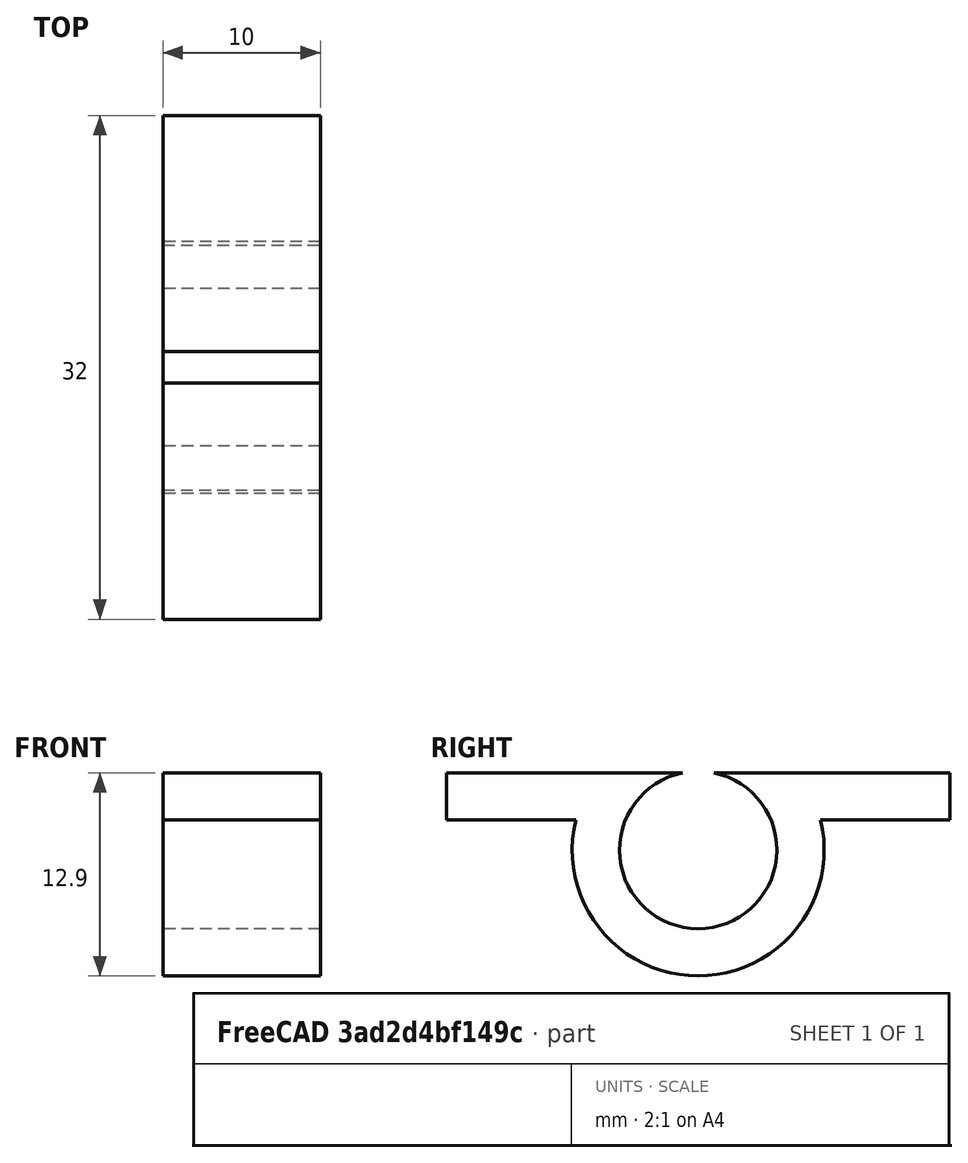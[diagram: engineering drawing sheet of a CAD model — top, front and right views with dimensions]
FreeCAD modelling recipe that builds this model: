
FCSTD DOCUMENT  (FreeCAD 0.16R6703 (Git))
Label: seesaw_hinge
License: Public Domain
LicenseURL: http://en.wikipedia.org/wiki/Public_domain
objects: Sketcher::SketchObject×1, PartDesign::Pad×1
note: 3 computed .brp shape members not serialized (recipe doc carries the construction recipe); baked Part::Feature solids carry a one-line shape summary decoded from their .brp

FEATURE [Sketcher::SketchObject] Sketch
  Placement = pos=(0,0,0) rot=(0.57735,0.57735,0.57735;2.0944rad)
  sketch-geometry (13):
    g0: ArcOfCircle CenterX=0 CenterY=-4.89898 CenterZ=0 NormalX=0 NormalY=0 NormalZ=1 Radius=5 StartAngle=1.77215 EndAngle=7.65262
    g1: LineSegment StartX=-1 StartY=0 StartZ=0 EndX=-16 EndY=0 EndZ=0
    g2: LineSegment StartX=-16 StartY=0 StartZ=0 EndX=-16 EndY=-3 EndZ=0
    g3: LineSegment StartX=-16 StartY=-3 StartZ=0 EndX=-7.77135 EndY=-3 EndZ=0
    g4: LineSegment StartX=1 StartY=0 StartZ=0 EndX=16 EndY=0 EndZ=0
    g5: LineSegment StartX=16 StartY=0 StartZ=0 EndX=16 EndY=-3 EndZ=0
    g6: LineSegment StartX=16 StartY=-3 StartZ=0 EndX=7.77135 EndY=-3 EndZ=0
    g7: ArcOfCircle CenterX=0 CenterY=-4.89898 CenterZ=0 NormalX=0 NormalY=0 NormalZ=1 Radius=8 StartAngle=2.90193 EndAngle=6.52285
    g8: LineSegment [constr] StartX=-1 StartY=0 StartZ=0 EndX=1 EndY=0 EndZ=0
    g9: GeomPoint [constr] X=-3.47116 Y=-8.49773 Z=0
    g10: LineSegment [constr] StartX=0 StartY=-4.89898 StartZ=0 EndX=-3.47116 EndY=-8.49773 EndZ=0
    g11: LineSegment [constr] StartX=-3.47116 StartY=-8.49773 StartZ=0 EndX=-5.55386 EndY=-10.657 EndZ=0
    g12: LineSegment [constr] StartX=0 StartY=-4.89898 StartZ=0 EndX=0 EndY=0 EndZ=0
  constraints (35):
    c: Coincident(g1,g0)
    c: Coincident(g2,g1)
    c: Coincident(g3,g2)
    c: Coincident(g4,g0)
    c: Coincident(g5,g4)
    c: Coincident(g6,g5)
    c: Coincident(g7,g0)
    c: Coincident(g7,g3)
    c: Coincident(g7,g6)
    c: Horizontal(g1)
    c: Horizontal(g4)
    c: Horizontal(g6)
    c: Horizontal(g3)
    c: Vertical(g2)
    c: Vertical(g5)
    c: Equal(g5,g2)
    c: Equal(g4,g1)
    c: Coincident(g8,g0)
    c: Coincident(g8,g0)
    c: Horizontal(g8)
    c: PointOnObject(g9,g0)
    c: Coincident(g10,g0)
    c: Coincident(g10,g9)
    c: Coincident(g11,g9)
    c: PointOnObject(g11,g7)
    c: Parallel(g11,g10)
    c: Equal(g2,g11)
    c: DistanceX(g4,g4) = 15
    c: DistanceY(g5,g5) = 3
    c: Coincident(g12,g0)
    c: PointOnObject(g12,g8)
    c: Vertical(g12)
    c: Distance(g10) = 5
    c: Coincident(g12,g-1)  'final_anchor'
    c: DistanceX(g8,g8) = 2
FEATURE [PartDesign::Pad] Pad
  Length = 10
  Length2 = 100
  Placement = pos=(0,0,0) rot=(0.57735,0.57735,0.57735;2.0944rad)
  Sketch = -> Sketch
  Type = 0
